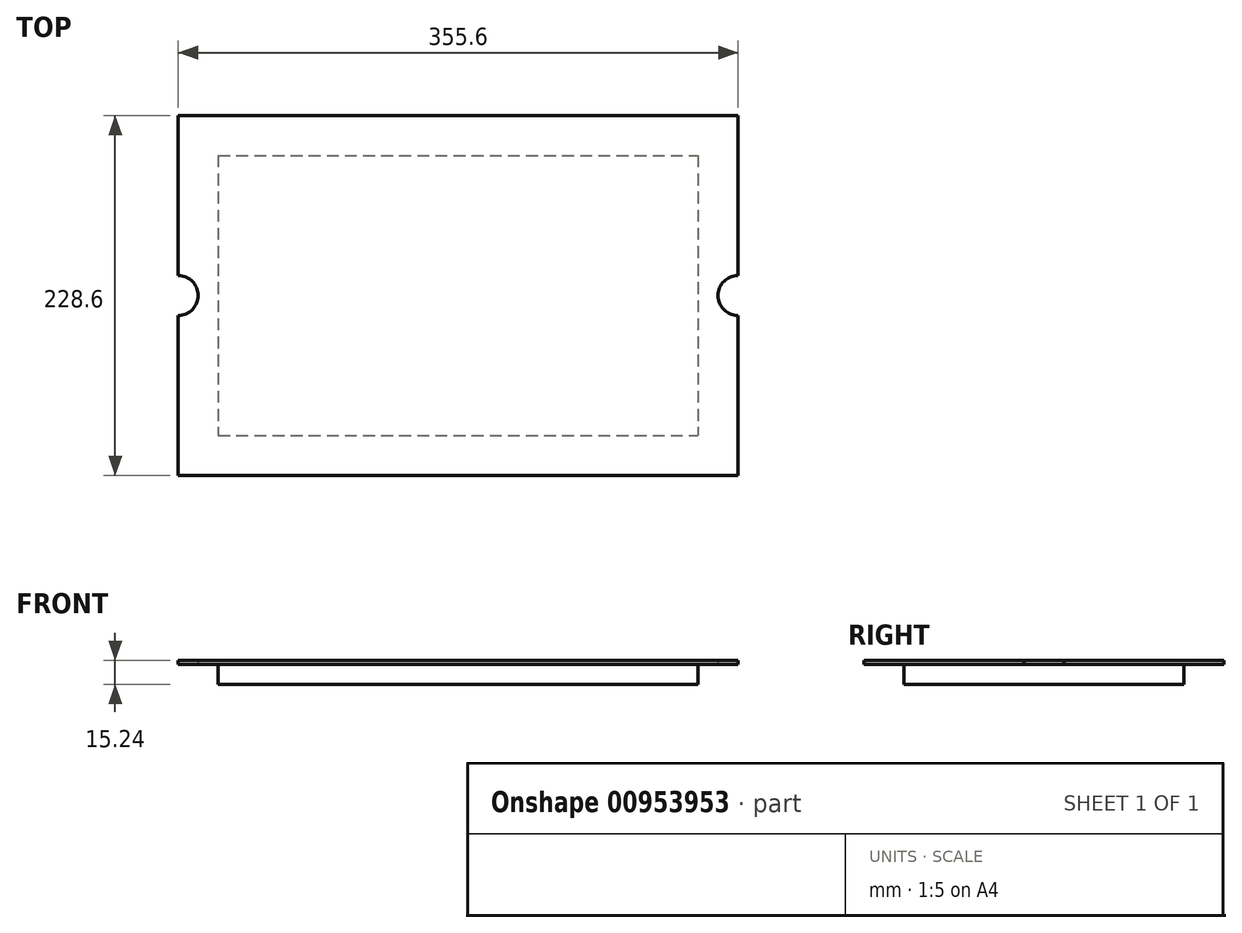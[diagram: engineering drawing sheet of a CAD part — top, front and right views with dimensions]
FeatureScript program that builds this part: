
annotation { "Feature Type Name" : "Feature", "Feature Type Description" : "" }
export const myFeature = defineFeature(function(context is Context, id is Id, definition is map)
    precondition{}
    {
        {
            var Q0;
            Q0=qCreatedBy(makeId("Top.planeOp"),FACE);
            var sketch = newSketch(context, id + "F0", { "sketchPlane" : qUnion([Q0])});
            skLineSegment(sketch, "E0.bottom", {"start": v(-177.8, 114.3) * mm, "end": v(177.8, 114.3) * mm});
            skLineSegment(sketch, "E0.top", {"start": v(-177.8, -114.3) * mm, "end": v(177.8, -114.3) * mm});
            skLineSegment(sketch, "E0.left", {"start": v(-177.8, 114.3) * mm, "end": v(-177.8, 12.7) * mm});
            skLineSegment(sketch, "E0.right", {"start": v(177.8, 114.3) * mm, "end": v(177.8, 12.7) * mm});
            skPoint(sketch, "E0.middle", {"position": v(0, 0) * mm});
            skArc(sketch, "E1", {"start": v(-177.8, -12.7) * mm, "mid": v(-165.1, 0) * mm, "end": v(-177.8, 12.7) * mm});
            skArc(sketch, "E2", {"start": v(177.8, 12.7) * mm, "mid": v(165.1, 0) * mm, "end": v(177.8, -12.7) * mm});
            skLineSegment(sketch, "E3.trimOffspring", {"start": v(-177.8, -12.7) * mm, "end": v(-177.8, -114.3) * mm});
            skLineSegment(sketch, "E4.trimOffspring", {"start": v(177.8, -12.7) * mm, "end": v(177.8, -114.3) * mm});
            skSolve(sketch);
        }
        {
            var Q0;
            Q0 = qSketchRegion(id + "F0", true);
            extrude(context, id + "F1", {"entities" : qUnion([Q0]), "depth" : 2.54 * mm, "offsetDistance" : 25.4 * mm});
        }
        {
            var Q0;
            Q0=makeQuery(id+"F1.opExtrude","CAP_FACE",FACE,{"disambiguationData":[OSD([sQuery(id+"F0.wireOp",EDGE,"E0.bottom"),sQuery(id+"F0.wireOp",EDGE,"E0.top"),sQuery(id+"F0.wireOp",EDGE,"E0.left"),sQuery(id+"F0.wireOp",EDGE,"E0.right"),sQuery(id+"F0.wireOp",EDGE,"E1"),sQuery(id+"F0.wireOp",EDGE,"E2"),sQuery(id+"F0.wireOp",EDGE,"E3.trimOffspring"),sQuery(id+"F0.wireOp",EDGE,"E4.trimOffspring")])],"isStart":true});
            var sketch = newSketch(context, id + "F2", { "sketchPlane" : qUnion([Q0])});
            skLineSegment(sketch, "E5.bottom", {"start": v(-152.4, -88.9) * mm, "end": v(152.4, -88.9) * mm});
            skLineSegment(sketch, "E5.top", {"start": v(-152.4, 88.9) * mm, "end": v(152.4, 88.9) * mm});
            skLineSegment(sketch, "E5.left", {"start": v(-152.4, -88.9) * mm, "end": v(-152.4, 88.9) * mm});
            skLineSegment(sketch, "E5.right", {"start": v(152.4, -88.9) * mm, "end": v(152.4, 88.9) * mm});
            skPoint(sketch, "E5.middle", {"position": v(0, 0) * mm});
            skSolve(sketch);
        }
        {
            var Q0;
            Q0 = qSketchRegion(id + "F2", true);
            extrude(context, id + "F3", {"entities" : qUnion([Q0]), "operationType" : NewBodyOperationType.ADD, "depth" : 12.7 * mm, "offsetDistance" : 25.4 * mm});
        }
    });
